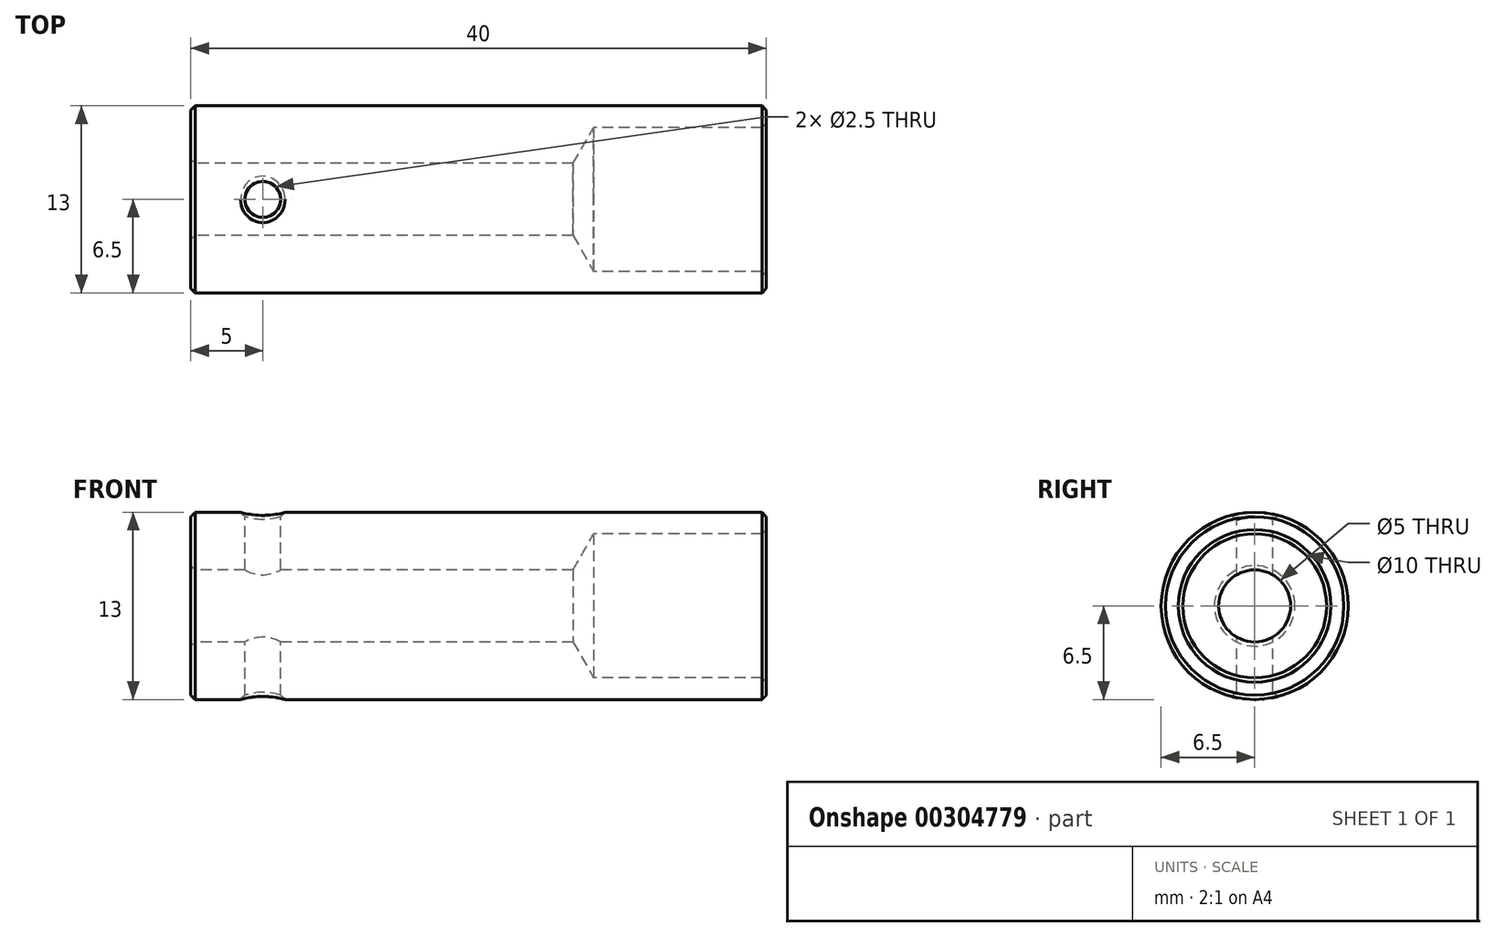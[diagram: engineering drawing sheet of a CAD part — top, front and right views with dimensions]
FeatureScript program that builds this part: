
annotation { "Feature Type Name" : "Feature", "Feature Type Description" : "" }
export const myFeature = defineFeature(function(context is Context, id is Id, definition is map)
    precondition{}
    {
        {
            assignVariable(context, id + "F0", {"name" : "dia", "anyValue" : 13 * mm});
        }
        {
            var Q0;
            Q0=qCreatedBy(makeId("Front.planeOp"),FACE);
            var sketch = newSketch(context, id + "F1", { "sketchPlane" : qUnion([Q0])});
            skLineSegment(sketch, "E0", {"start": v(0, 2.5) * mm, "end": v(0, 6.5) * mm});
            skLineSegment(sketch, "E1", {"start": v(0, 6.5) * mm, "end": v(40, 6.5) * mm});
            skLineSegment(sketch, "E2", {"start": v(40, 6.5) * mm, "end": v(40, 5) * mm});
            skLineSegment(sketch, "E3", {"start": v(40, 5) * mm, "end": v(28, 5) * mm});
            skLineSegment(sketch, "E4", {"start": v(28, 5) * mm, "end": v(26.56, 2.5) * mm});
            skLineSegment(sketch, "E5", {"start": v(26.56, 2.5) * mm, "end": v(0, 2.5) * mm});
            skLineSegment(sketch, "E6", {"start": v(-55.78, 0) * mm, "end": v(-14.46, 0) * mm, "construction": true});
            skSolve(sketch);
        }
        {
            var Q0;
            Q0=makeQuery(id+"F1.imprint","IMPRINT",FACE,{"disambiguationData":[TD([[makeQuery(id+"F1.imprint","IMPRINT",EDGE,{"derivedFrom":sQuery(id+"F1.wireOp",EDGE,"E0")}),-1.0]])]});
            var Q1;
            Q1=sQuery(id+"F1.wireOp",EDGE,"E6");
            revolve(context, id + "F2", {"entities" : qUnion([Q0]), "axis" : qUnion([Q1]), "revolveType" : RevolveType.FULL});
        }
        {
            var Q0;
            Q0=qCreatedBy(makeId("Top.planeOp"),FACE);
            var sketch = newSketch(context, id + "F3", { "sketchPlane" : qUnion([Q0])});
            skCircle(sketch, "E7", {"center": v(5, 0) * mm, "radius": 1.25 * mm});
            skSolve(sketch);
        }
        {
            var Q0;
            Q0=makeQuery(id+"F3.imprint","IMPRINT",FACE,{"disambiguationData":[TD([[makeQuery(id+"F3.imprint","IMPRINT",EDGE,{"derivedFrom":sQuery(id+"F3.wireOp",EDGE,"E7")}),1.0]])]});
            extrude(context, id + "F4", {"entities" : qUnion([Q0]), "operationType" : NewBodyOperationType.REMOVE, "endBound" : BoundingType.SYMMETRIC, "oppositeDirection" : true, "depth" : getVariable(context, 'dia')});
        }
        {
            var Q0;
            Q0=makeQuery(id+"F2.opRevolve","SWEPT_EDGE",EDGE,{"disambiguationData":[OSD([sQuery(id+"F1.wireOp",EDGE,"E0"),sQuery(id+"F1.wireOp",EDGE,"E1")])]});
            var Q1;
            Q1=makeQuery(id+"F2.opRevolve","SWEPT_EDGE",EDGE,{"disambiguationData":[OSD([sQuery(id+"F1.wireOp",EDGE,"E0"),sQuery(id+"F1.wireOp",EDGE,"E5")])]});
            var Q2;
            Q2=makeQuery(id+"F2.opRevolve","SWEPT_EDGE",EDGE,{"disambiguationData":[OSD([sQuery(id+"F1.wireOp",EDGE,"E1"),sQuery(id+"F1.wireOp",EDGE,"E2")])]});
            var Q3;
            Q3=makeQuery(id+"F2.opRevolve","SWEPT_EDGE",EDGE,{"disambiguationData":[OSD([sQuery(id+"F1.wireOp",EDGE,"E2"),sQuery(id+"F1.wireOp",EDGE,"E3")])]});
            var Q4;
            Q4=makeQuery(id+"F4.boolean.opBoolean","INTERSECT",EDGE,{"disambiguationData":[OD(1.0)],"derivedFrom":[makeQuery(id+"F2.opRevolve","SWEPT_FACE",FACE,{"disambiguationData":[OSD([sQuery(id+"F1.wireOp",EDGE,"E1")])]}),makeQuery(id+"F4.opExtrude","SWEPT_FACE",FACE,{"disambiguationData":[OSD([sQuery(id+"F3.wireOp",EDGE,"E7")])]})]});
            var Q5;
            Q5=makeQuery(id+"F4.boolean.opBoolean","INTERSECT",EDGE,{"disambiguationData":[OD(0.0)],"derivedFrom":[makeQuery(id+"F2.opRevolve","SWEPT_FACE",FACE,{"disambiguationData":[OSD([sQuery(id+"F1.wireOp",EDGE,"E1")])]}),makeQuery(id+"F4.opExtrude","SWEPT_FACE",FACE,{"disambiguationData":[OSD([sQuery(id+"F3.wireOp",EDGE,"E7")])]})]});
            chamfer(context, id + "F5", {"entities" : qUnion([Q0, Q1, Q2, Q3, Q4, Q5]), "width" : 0.3 * mm, "tangentPropagation" : true});
        }
    });
